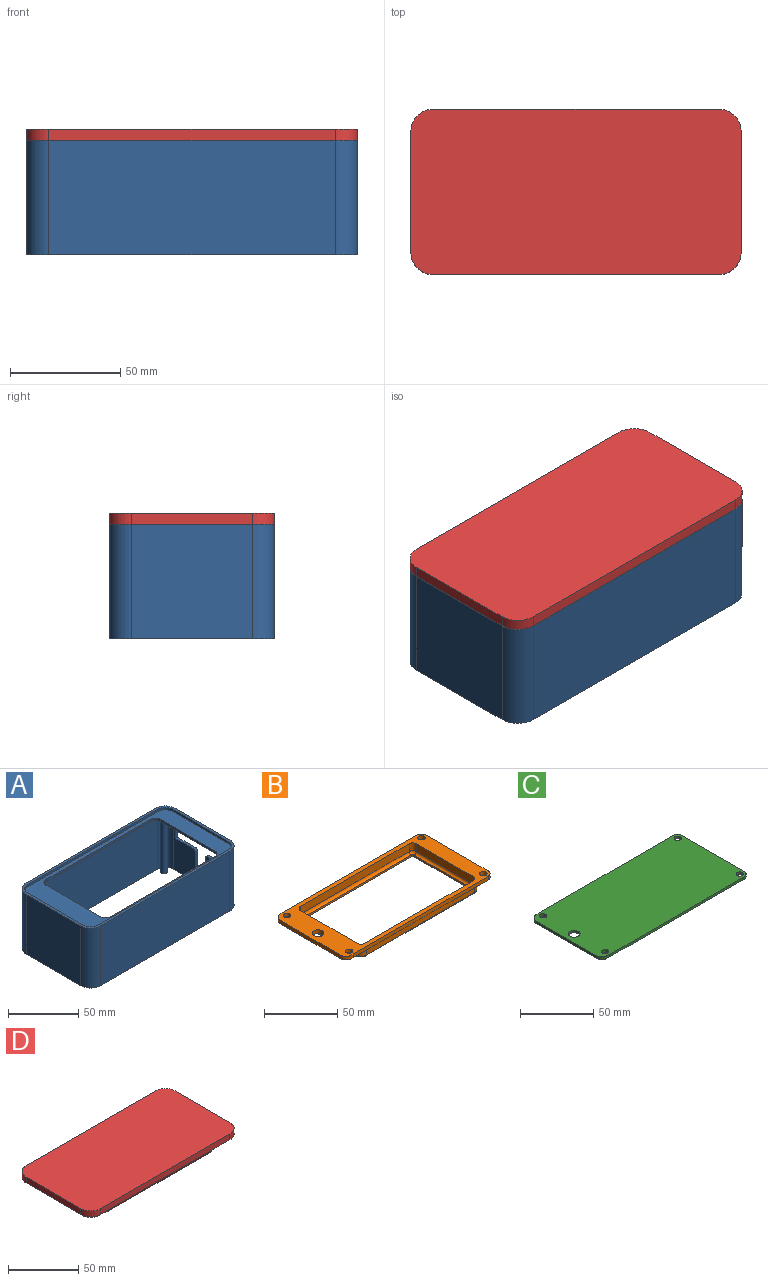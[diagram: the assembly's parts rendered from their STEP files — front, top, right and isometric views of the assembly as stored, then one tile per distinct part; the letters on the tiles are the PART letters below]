
ASSEMBLY  parts=4 mates=5
PART A: 60 faces, bbox 150x75x52 mm
  f0: plane 150x75mm, normal (0,0,-1), area 853.1mm2, adj f1,f2,f3,f4,f6,f7,f8,f9
  f1: plane 130x52mm, normal (0,1,0), area 6760mm2, adj f0,f6,f9,f59
  f2: plane 55x52mm, normal (1,0,0), area 2110.4mm2, adj f0,f6,f7,f37,f38,f39,f40,f41
  f3: plane 130x52mm, normal (0,-1,0), area 6760mm2, adj f0,f7,f8,f59
  f4: plane 55x52mm, normal (-1,0,0), area 2860mm2, adj f0,f8,f9,f59
  f5: plane 146x71mm, normal (0,0,1), area 2857.5mm2, adj f19,f20,f21,f22,f23,f24,f25,f26
  f6: cylinder r=10mm len=52mm, axis (0,0,-1), area 816.8mm2, adj f0,f1,f2,f59
  f7: cylinder r=10mm len=52mm, axis (0,0,1), area 816.8mm2, adj f0,f2,f3,f59
  f8: cylinder r=10mm len=52mm, axis (0,0,-1), area 816.8mm2, adj f0,f3,f4,f59
  f9: cylinder r=10mm len=52mm, axis (0,0,1), area 816.8mm2, adj f0,f1,f4,f59
  f10: plane 130x48mm, normal (0,-1,0), area 6240mm2, adj f0,f14,f15,f18
  f11: plane 55x48mm, normal (-1,0,0), area 1890.4mm2, adj f0,f14,f15,f16,f37,f38,f39,f40
  f12: plane 130x48mm, normal (0,1,0), area 6240mm2, adj f0,f14,f16,f17
  f13: plane 55x48mm, normal (1,0,0), area 2640mm2, adj f0,f14,f17,f18
  f14: plane 146x71mm, normal (0,0,-1), area 2728.7mm2, adj f10,f11,f12,f13,f15,f16,f17,f18
  f15: cylinder r=8mm len=48mm, axis (0,0,-1), area 603.2mm2, adj f0,f10,f11,f14
  f16: cylinder r=8mm len=48mm, axis (0,0,1), area 603.2mm2, adj f0,f11,f12,f14
  f17: cylinder r=8mm len=48mm, axis (0,0,-1), area 603.2mm2, adj f0,f12,f13,f14
  f18: cylinder r=8mm len=48mm, axis (0,0,1), area 603.2mm2, adj f0,f10,f13,f14
  f19: plane 55x2mm, normal (-1,0,0), area 110mm2, adj f5,f14,f20,f26
  f20: cylinder r=5mm len=5mm, axis (0,0,-1), area 15.7mm2, adj f5,f14,f19,f21
  f21: plane 105x2mm, normal (0,1,0), area 210mm2, adj f5,f14,f20,f22
  f22: cylinder r=5mm len=5mm, axis (0,0,-1), area 15.7mm2, adj f5,f14,f21,f23
  f23: plane 55x2mm, normal (1,0,0), area 110mm2, adj f5,f14,f22,f24
  f24: cylinder r=5mm len=5mm, axis (0,0,-1), area 15.7mm2, adj f5,f14,f23,f25
  f25: plane 105x2mm, normal (0,-1,0), area 210mm2, adj f5,f14,f24,f26
  f26: cylinder r=5mm len=5mm, axis (0,0,-1), area 15.7mm2, adj f5,f14,f19,f25
  f27: cylinder r=4mm len=48mm, axis (0,0,1), area 1206.4mm2, adj f14,f28
  f28: plane 8x8mm, normal (0,0,-1), area 50.3mm2, adj f27
  f29: cylinder r=2.5mm len=48mm, axis (0,0,1), area 754mm2, adj f14,f30
  f30: plane 5x5mm, normal (0,0,-1), area 19.6mm2, adj f29
  f31: cylinder r=2.5mm len=48mm, axis (0,0,1), area 754mm2, adj f14,f32
  f32: plane 5x5mm, normal (0,0,-1), area 19.6mm2, adj f31
  f33: cylinder r=2.5mm len=48mm, axis (0,0,1), area 754mm2, adj f14,f34
  f34: plane 5x5mm, normal (0,0,-1), area 19.6mm2, adj f33
  f35: cylinder r=2.5mm len=48mm, axis (0,0,1), area 754mm2, adj f14,f36
  f36: plane 5x5mm, normal (0,0,-1), area 19.6mm2, adj f35
  f37: cylinder r=1mm len=2mm, axis (1,0,0), area 3.1mm2, adj f2,f11,f38,f50
  f38: plane 48x2mm, normal (0,0,-1), area 96mm2, adj f2,f11,f37,f39
  f39: cylinder r=1mm len=2mm, axis (1,0,0), area 3.1mm2, adj f2,f11,f38,f40
  f40: plane 9x2mm, normal (0,1,0), area 18mm2, adj f2,f11,f39,f41
  f41: plane 18x2mm, normal (0,0,1), area 36mm2, adj f2,f11,f40,f42
  f42: cylinder r=2mm len=2mm, axis (1,0,0), area 6.3mm2, adj f2,f11,f41,f43
  f43: plane 21x2mm, normal (0,1,0), area 42mm2, adj f2,f11,f42,f44
  f44: cylinder r=2mm len=2mm, axis (1,0,0), area 6.3mm2, adj f2,f11,f43,f45
  f45: plane 6x2mm, normal (0,0,1), area 12mm2, adj f2,f11,f44,f46
  f46: cylinder r=2mm len=2mm, axis (1,0,0), area 6.3mm2, adj f2,f11,f45,f47
  f47: plane 21x2mm, normal (0,-1,0), area 42mm2, adj f2,f11,f46,f48
  f48: cylinder r=2mm len=2mm, axis (1,0,0), area 6.3mm2, adj f2,f11,f47,f49
  f49: plane 18x2mm, normal (0,0,1), area 36mm2, adj f2,f11,f48,f50
  f50: plane 9x2mm, normal (0,-1,0), area 18mm2, adj f2,f11,f37,f49
  f51: cylinder r=8mm len=8mm, axis (0,0,-1), area 25.1mm2, adj f5,f52,f58,f59
  f52: plane 130x2mm, normal (0,1,0), area 260mm2, adj f5,f51,f53,f59
  f53: cylinder r=8mm len=8mm, axis (0,0,-1), area 25.1mm2, adj f5,f52,f54,f59
  f54: plane 55x2mm, normal (1,0,0), area 110mm2, adj f5,f53,f55,f59
  f55: cylinder r=8mm len=8mm, axis (0,0,-1), area 25.1mm2, adj f5,f54,f56,f59
  f56: plane 130x2mm, normal (0,-1,0), area 260mm2, adj f5,f55,f57,f59
  f57: cylinder r=8mm len=8mm, axis (0,0,-1), area 25.1mm2, adj f5,f56,f58,f59
  f58: plane 55x2mm, normal (-1,0,0), area 110mm2, adj f5,f51,f57,f59
  f59: plane 150x75mm, normal (0,0,1), area 853.1mm2, adj f1,f2,f3,f4,f6,f7,f8,f9
PART B: 60 faces, bbox 142x69x10 mm
  f0: plane 2x2mm, normal (0,0,1), area 0.4mm2, adj f40,f42,f43,f45
  f1: plane 2x2mm, normal (0,0,1), area 0.4mm2, adj f36,f38,f40,f47
  f2: plane 2x2mm, normal (0,0,1), area 0.4mm2, adj f36,f37,f39,f49
  f3: plane 2x2mm, normal (0,0,1), area 0.4mm2, adj f39,f41,f43,f51
  f4: plane 60x3mm, normal (-1,0,0), area 180mm2, adj f5,f16,f17,f18
  f5: extruded ~7.5x4.5mm, area 29.1mm2, adj f4,f6,f17,f18
  f6: plane 130x3mm, normal (0,1,0), area 390mm2, adj f5,f7,f17,f18
  f7: cylinder r=4.5mm len=4.5mm, axis (0,0,1), area 21.2mm2, adj f6,f8,f17,f18
  f8: plane 60x3mm, normal (1,0,0), area 180mm2, adj f7,f9,f17,f18
  f9: cylinder r=4.5mm len=4.5mm, axis (0,0,1), area 21.2mm2, adj f8,f10,f17,f18
  f10: plane 130x3mm, normal (0,-1,0), area 390mm2, adj f9,f16,f17,f18
  f11: cylinder r=2.5mm len=5mm, axis (0,0,1), area 47.1mm2, adj f17,f18
  f12: cylinder r=2.5mm len=5mm, axis (0,0,1), area 47.1mm2, adj f17,f18
  f13: cylinder r=2.5mm len=5mm, axis (0,0,1), area 47.1mm2, adj f17,f18
  f14: cylinder r=4mm len=8mm, axis (0,0,1), area 75.4mm2, adj f17,f18
  f15: cylinder r=2.5mm len=5mm, axis (0,0,1), area 47.1mm2, adj f17,f18
  f16: extruded ~7.5x4.5mm, area 29.1mm2, adj f4,f10,f17,f18
  f17: plane 142x69.04mm, normal (0,0,-1), area 2194.4mm2, adj f4,f5,f6,f7,f8,f9,f10,f11
  f18: plane 142x69.04mm, normal (0,0,1), area 2714.4mm2, adj f4,f5,f6,f7,f8,f9,f10,f11
  f19: plane 113x63mm, normal (0,0,-1), area 844.7mm2, adj f44,f45,f46,f47,f48,f49,f50,f51
  f20: cylinder r=5mm len=6mm, axis (0,0,1), area 47.1mm2, adj f17,f21,f27,f58
  f21: plane 105x6mm, normal (0,1,0), area 630mm2, adj f17,f20,f22,f56
  f22: cylinder r=5mm len=6mm, axis (0,0,1), area 47.1mm2, adj f17,f21,f23,f54
  f23: plane 55x6mm, normal (-1,0,0), area 330mm2, adj f17,f22,f24,f52
  f24: cylinder r=5mm len=6mm, axis (0,0,1), area 47.1mm2, adj f17,f23,f25,f53
  f25: plane 105x6mm, normal (0,-1,0), area 630mm2, adj f17,f24,f26,f55
  f26: cylinder r=5mm len=6mm, axis (0,0,1), area 47.1mm2, adj f17,f25,f27,f57
  f27: plane 55x6mm, normal (1,0,0), area 330mm2, adj f17,f20,f26,f59
  f28: plane 55x6.5mm, normal (-1,0,0), area 357.5mm2, adj f18,f29,f35,f43
  f29: cylinder r=3.5mm len=6.5mm, axis (0,0,1), area 35.7mm2, adj f18,f28,f30,f41
  f30: plane 105x6.5mm, normal (0,1,0), area 682.5mm2, adj f18,f29,f31,f39
  f31: cylinder r=3.5mm len=6.5mm, axis (0,0,1), area 35.7mm2, adj f18,f30,f32,f37
  f32: plane 55x6.5mm, normal (1,0,0), area 357.5mm2, adj f18,f31,f33,f36
  f33: cylinder r=3.5mm len=6.5mm, axis (0,0,1), area 35.7mm2, adj f18,f32,f34,f38
  f34: plane 105x6.5mm, normal (0,-1,0), area 682.5mm2, adj f18,f33,f35,f40
  f35: cylinder r=3.5mm len=6.5mm, axis (0,0,1), area 35.7mm2, adj f18,f28,f34,f42
  f36: cylinder r=2mm len=55mm, axis (0,1,0), area 172.8mm2, adj f1,f2,f32,f37,f38,f48
  f37: torus R=1.5mm, axis (0,0,-1), area 13.7mm2, adj f2,f31,f36,f39
  f38: torus R=1.5mm, axis (0,0,-1), area 13.7mm2, adj f1,f33,f36,f40
  f39: cylinder r=2mm len=105mm, axis (-1,0,0), area 329.9mm2, adj f2,f3,f30,f37,f41,f50
  f40: cylinder r=2mm len=105mm, axis (1,0,0), area 329.9mm2, adj f0,f1,f34,f38,f42,f46
  f41: torus R=1.5mm, axis (0,0,-1), area 13.7mm2, adj f3,f29,f39,f43
  f42: torus R=1.5mm, axis (0,0,-1), area 13.7mm2, adj f0,f35,f40,f43
  f43: cylinder r=2mm len=55mm, axis (0,-1,0), area 172.8mm2, adj f0,f3,f28,f41,f42,f44
  f44: plane 54x1.5mm, normal (-1,0,0), area 81mm2, adj f19,f43,f45,f51
  f45: cylinder r=2mm len=2mm, axis (0,0,1), area 4.7mm2, adj f0,f19,f44,f46
  f46: plane 104x1.5mm, normal (0,-1,0), area 156mm2, adj f19,f40,f45,f47
  f47: cylinder r=2mm len=2mm, axis (0,0,1), area 4.7mm2, adj f1,f19,f46,f48
  f48: plane 54x1.5mm, normal (1,0,0), area 81mm2, adj f19,f36,f47,f49
  f49: cylinder r=2mm len=2mm, axis (0,0,1), area 4.7mm2, adj f2,f19,f48,f50
  f50: plane 104x1.5mm, normal (0,1,0), area 156mm2, adj f19,f39,f49,f51
  f51: cylinder r=2mm len=2mm, axis (0,0,1), area 4.7mm2, adj f3,f19,f44,f50
  f52: cylinder r=1mm len=55mm, axis (0,-1,0), area 86.4mm2, adj f19,f23,f53,f54
  f53: torus R=4mm, axis (0,0,-1), area 11.4mm2, adj f19,f24,f52,f55
  f54: torus R=4mm, axis (0,0,-1), area 11.4mm2, adj f19,f22,f52,f56
  f55: cylinder r=1mm len=105mm, axis (1,0,0), area 164.9mm2, adj f19,f25,f53,f57
  f56: cylinder r=1mm len=105mm, axis (-1,0,0), area 164.9mm2, adj f19,f21,f54,f58
  f57: torus R=4mm, axis (0,0,-1), area 11.4mm2, adj f19,f26,f55,f59
  f58: torus R=4mm, axis (0,0,-1), area 11.4mm2, adj f19,f20,f56,f59
  f59: cylinder r=1mm len=55mm, axis (0,1,0), area 86.4mm2, adj f19,f27,f57,f58
PART C: 17 faces, bbox 142x69x2 mm
  f0: cylinder r=5mm len=5mm, axis (0,0,-1), area 15.7mm2, adj f1,f13,f15,f16
  f1: plane 59x2mm, normal (1,0,0), area 118mm2, adj f0,f2,f15,f16
  f2: cylinder r=5mm len=5mm, axis (0,0,-1), area 15.7mm2, adj f1,f3,f15,f16
  f3: plane 129.5x2mm, normal (0,1,0), area 259mm2, adj f2,f4,f15,f16
  f4: extruded ~7.38x3.93mm, area 18.2mm2, adj f3,f5,f15,f16
  f5: cylinder r=5mm len=2mm, axis (0,0,-1), area 2.2mm2, adj f4,f6,f15,f16
  f6: plane 59x2mm, normal (-1,0,0), area 118mm2, adj f5,f7,f15,f16
  f7: cylinder r=5mm len=2mm, axis (0,0,-1), area 2.2mm2, adj f6,f8,f15,f16
  f8: extruded ~7.38x3.93mm, area 18.2mm2, adj f7,f13,f15,f16
  f9: cylinder r=2.5mm len=5mm, axis (0,0,-1), area 31.4mm2, adj f15,f16
  f10: cylinder r=4mm len=8mm, axis (0,0,-1), area 50.3mm2, adj f15,f16
  f11: cylinder r=2.5mm len=5mm, axis (0,0,-1), area 31.4mm2, adj f15,f16
  f12: cylinder r=2.5mm len=5mm, axis (0,0,-1), area 31.4mm2, adj f15,f16
  f13: plane 129.5x2mm, normal (0,-1,0), area 259mm2, adj f0,f8,f15,f16
  f14: cylinder r=2.5mm len=5mm, axis (0,0,-1), area 31.4mm2, adj f15,f16
  f15: plane 142x69.04mm, normal (0,0,1), area 9645.9mm2, adj f0,f1,f2,f3,f4,f5,f6,f7
  f16: plane 142x69.04mm, normal (0,0,-1), area 9645.9mm2, adj f0,f1,f2,f3,f4,f5,f6,f7
PART D: 36 faces, bbox 150x75x17 mm
  f0: plane 146x71mm, normal (0,0,-1), area 3887.8mm2, adj f11,f12,f13,f14,f15,f16,f17,f18
  f1: plane 150x75mm, normal (0,0,-1), area 853.1mm2, adj f2,f3,f4,f5,f7,f8,f9,f10
  f2: plane 130x5mm, normal (0,-1,0), area 650mm2, adj f1,f6,f7,f10
  f3: plane 55x5mm, normal (1,0,0), area 275mm2, adj f1,f6,f7,f8
  f4: plane 130x5mm, normal (0,1,0), area 650mm2, adj f1,f6,f8,f9
  f5: plane 55x5mm, normal (-1,0,0), area 275mm2, adj f1,f6,f9,f10
  f6: plane 150x75mm, normal (0,0,1), area 11164.2mm2, adj f2,f3,f4,f5,f7,f8,f9,f10
  f7: cylinder r=10mm len=10mm, axis (0,0,1), area 78.5mm2, adj f1,f2,f3,f6
  f8: cylinder r=10mm len=10mm, axis (0,0,-1), area 78.5mm2, adj f1,f3,f4,f6
  f9: cylinder r=10mm len=10mm, axis (0,0,1), area 78.5mm2, adj f1,f4,f5,f6
  f10: cylinder r=10mm len=10mm, axis (0,0,-1), area 78.5mm2, adj f1,f2,f5,f6
  f11: cylinder r=8mm len=8mm, axis (0,0,1), area 25.1mm2, adj f0,f1,f12,f18
  f12: plane 55x2mm, normal (-1,0,0), area 110mm2, adj f0,f1,f11,f13
  f13: cylinder r=8mm len=8mm, axis (0,0,1), area 25.1mm2, adj f0,f1,f12,f14
  f14: plane 130x2mm, normal (0,1,0), area 260mm2, adj f0,f1,f13,f15
  f15: cylinder r=8mm len=8mm, axis (0,0,1), area 25.1mm2, adj f0,f1,f14,f16
  f16: plane 55x2mm, normal (1,0,0), area 110mm2, adj f0,f1,f15,f17
  f17: cylinder r=8mm len=8mm, axis (0,0,1), area 25.1mm2, adj f0,f1,f16,f18
  f18: plane 130x2mm, normal (0,-1,0), area 260mm2, adj f0,f1,f11,f17
  f19: plane 103x5mm, normal (0,1,0), area 515mm2, adj f0,f20,f26,f32
  f20: cylinder r=3mm len=5mm, axis (0,0,1), area 23.6mm2, adj f0,f19,f21,f34
  f21: plane 53x5mm, normal (1,0,0), area 265mm2, adj f0,f20,f22,f35
  f22: cylinder r=3mm len=5mm, axis (0,0,1), area 23.6mm2, adj f0,f21,f23,f33
  f23: plane 103x5mm, normal (0,-1,0), area 515mm2, adj f0,f22,f24,f31
  f24: cylinder r=3mm len=5mm, axis (0,0,1), area 23.6mm2, adj f0,f23,f25,f29
  f25: plane 53x5mm, normal (-1,0,0), area 265mm2, adj f0,f24,f26,f28
  f26: cylinder r=3mm len=5mm, axis (0,0,1), area 23.6mm2, adj f0,f19,f25,f30
  f27: plane 99x49mm, normal (0,0,-1), area 4851mm2, adj f28,f31,f32,f35
  f28: cylinder r=5mm len=53mm, axis (0,-1,0), area 404.8mm2, adj f25,f27,f29,f30
  f29: bspline ~6.03x5mm, area 24.5mm2, adj f24,f28,f31
  f30: bspline ~6.03x5mm, area 24.5mm2, adj f26,f28,f32
  f31: cylinder r=5mm len=103mm, axis (1,0,0), area 797.5mm2, adj f23,f27,f29,f33
  f32: cylinder r=5mm len=103mm, axis (-1,0,0), area 797.5mm2, adj f19,f27,f30,f34
  f33: bspline ~6.03x5mm, area 24.5mm2, adj f22,f31,f35
  f34: bspline ~6.03x5mm, area 24.5mm2, adj f20,f32,f35
  f35: cylinder r=5mm len=53mm, axis (0,1,0), area 404.8mm2, adj f21,f27,f33,f34
PLACE A t=(0.61,0.65,0.13)mm fixed
PLACE B rot(axis=(0,0,1),0deg) t=(0.61,0.65,36.17)mm
PLACE C t=(0.61,0.65,22.87)mm
PLACE D t=(0.61,0.65,-22.67)mm
MATE slider B.f7 <-> A.f35  axis (0,0,1) through (66.61,30.65,-41.83)mm
MATE slider D.f8 <-> A.f6  axis (0,0,-1) through (65.61,28.15,-24.67)mm
MATE slider C.f11 <-> A.f33  axis (0,0,1) through (66.61,-29.35,-50.13)mm
MATE slider D.f7 <-> A.f7  axis (0,0,-1) through (65.61,-26.85,-24.67)mm
MATE slider B.f9 <-> A.f33  axis (0,0,-1) through (66.61,-29.35,-41.83)mm
